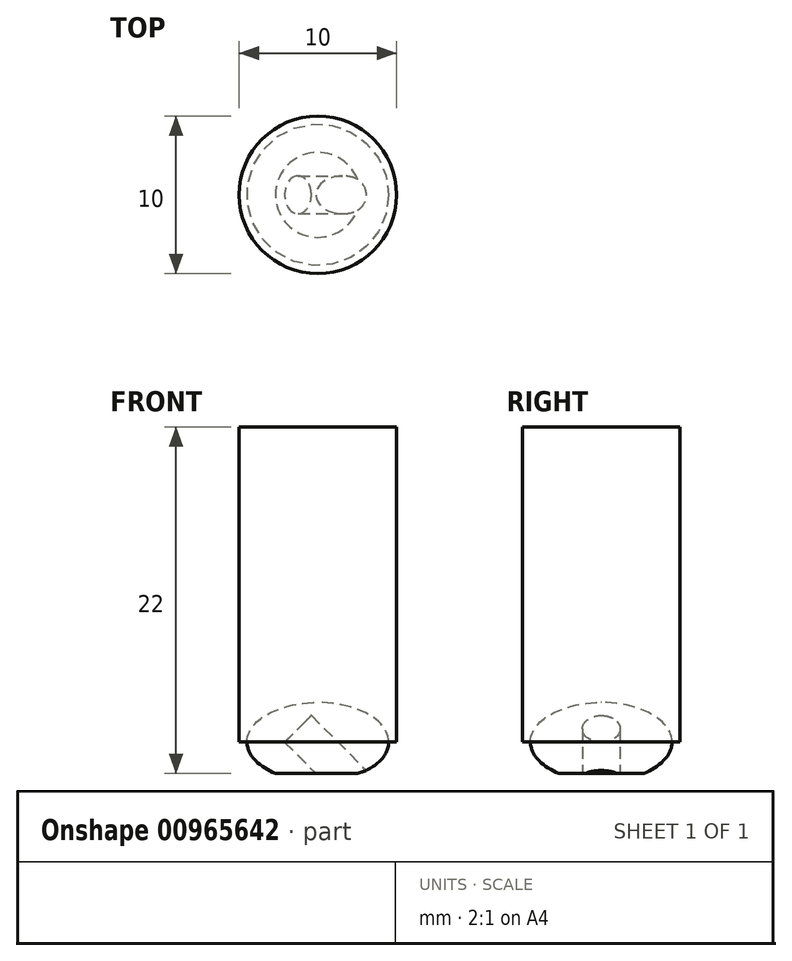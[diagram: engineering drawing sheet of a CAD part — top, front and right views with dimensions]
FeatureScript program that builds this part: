
annotation { "Feature Type Name" : "Feature", "Feature Type Description" : "" }
export const myFeature = defineFeature(function(context is Context, id is Id, definition is map)
    precondition{}
    {
        {
            var Q0;
            Q0=qCreatedBy(makeId("Front.planeOp"),FACE);
            var sketch = newSketch(context, id + "F0", { "sketchPlane" : qUnion([Q0])});
            skEllipse(sketch, "E0", {"center": v(0, 0) * mm, "majorRadius": 4.5 * mm, "minorRadius": 2.5 * mm, "majorAxis": v(1, 0)});
            skLineSegment(sketch, "E1", {"start": v(-2.7, -2) * mm, "end": v(2.7, -2) * mm});
            skLineSegment(sketch, "E2", {"start": v(-1.26, 0.83) * mm, "end": v(3.01, -3.45) * mm, "construction": true});
            skLineSegment(sketch, "E3", {"start": v(-1.26, 0.83) * mm, "end": v(-0.41, 1.68) * mm});
            skLineSegment(sketch, "E4.MirrorCS", {"start": v(-1.26, 0.83) * mm, "end": v(-2.11, -0.02) * mm});
            skLineSegment(sketch, "E5", {"start": v(-0.41, 1.68) * mm, "end": v(3.86, -2.6) * mm});
            skLineSegment(sketch, "E6.MirrorCS", {"start": v(-2.11, -0.02) * mm, "end": v(2.16, -4.3) * mm});
            skPoint(sketch, "E7", {"position": v(1.57, -2) * mm});
            skLineSegment(sketch, "E8", {"start": v(0, 2.5) * mm, "end": v(0, -2) * mm});
            skLineSegment(sketch, "E9", {"start": v(0, -2) * mm, "end": v(0, -2.5) * mm, "construction": true});
            skSolve(sketch);
        }
        {
            var Q0;
            {var subQ0=sQuery(id+"F0.wireOp",EDGE,"E8");var subQ1=sQuery(id+"F0.wireOp",EDGE,"E1");var subQ2=makeQuery(id+"F0.imprint","INTERSECT",VERTEX,{"derivedFrom":[subQ1,subQ0]});Q0=makeQuery(id+"F0.imprint","IMPRINT",FACE,{"disambiguationData":[TD([[makeQuery(id+"F0.imprint","IMPRINT",EDGE,{"disambiguationData":[TD([[subQ2,-1.0]])],"derivedFrom":subQ1}),1.0]])]});}
            var Q1;
            {var subQ0=sQuery(id+"F0.wireOp",EDGE,"E8");var subQ1=sQuery(id+"F0.wireOp",EDGE,"E0");var subQ2=makeQuery(id+"F0.imprint","INTERSECT",VERTEX,{"derivedFrom":[subQ1,subQ0]});Q1=makeQuery(id+"F0.imprint","IMPRINT",FACE,{"disambiguationData":[TD([[makeQuery(id+"F0.imprint","IMPRINT",EDGE,{"disambiguationData":[TD([[subQ2,1.0]])],"derivedFrom":subQ1}),1.0]])]});}
            var Q2;
            {var subQ0=sQuery(id+"F0.wireOp",EDGE,"E5");var subQ3=sQuery(id+"F0.wireOp",EDGE,"E0");var subQ4=makeQuery(id+"F0.imprint","INTERSECT",VERTEX,{"derivedFrom":[subQ3,subQ0]});Q2=makeQuery(id+"F0.imprint","IMPRINT",FACE,{"disambiguationData":[TD([[makeQuery(id+"F0.imprint","IMPRINT",EDGE,{"disambiguationData":[TD([[subQ4,1.0]])],"derivedFrom":subQ3}),1.0]])]});}
            var Q3;
            Q3=sQuery(id+"F0.wireOp",EDGE,"E8");
            revolve(context, id + "F1", {"surfaceOperationType" : NewSurfaceOperationType.NEW, "entities" : qUnion([Q0, Q1, Q2]), "axis" : qUnion([Q3]), "revolveType" : RevolveType.FULL});
        }
        {
            var Q0;
            Q0=sQuery(id+"F0.wireOp",EDGE,"E2");
            var Q1;
            Q1=sQuery(id+"F0.wireOp",VERTEX,"E2.end");
            cPlane(context, id + "F2", {"entities" : qUnion([Q0, Q1]), "cplaneType" : CPlaneType.LINE_POINT, "offset" : 25 * mm, "width" : 150 * mm, "height" : 150 * mm});
        }
        {
            var Q0;
            Q0=qCreatedBy(id+"F2.planeOp",FACE);
            var sketch = newSketch(context, id + "F3", { "sketchPlane" : qUnion([Q0])});
            skCircle(sketch, "E10", {"center": v(0, -0.3) * mm, "radius": 1.2 * mm});
            skSolve(sketch);
        }
        {
            var Q0;
            Q0 = qSketchRegion(id + "F3", true);
            var Q1;
            Q1=sQuery(id+"F0.wireOp",VERTEX,"E2.start");
            extrude(context, id + "F4", {"entities" : qUnion([Q0]), "operationType" : NewBodyOperationType.REMOVE, "endBound" : BoundingType.UP_TO_VERTEX, "oppositeDirection" : true, "depth" : 25 * mm, "endBoundEntityVertex" : qUnion([Q1]), "offsetDistance" : 25 * mm});
        }
        {
            var Q0;
            Q0=qCreatedBy(makeId("Top.planeOp"), FACE);
            var sketch = newSketch(context, id + "F5", { "sketchPlane" : qUnion([Q0])});
            skCircle(sketch, "E11", {"center": v(0, 0) * mm, "radius": 5 * mm});
            skSolve(sketch);
        }
        {
            var Q0;
            Q0 = qSketchRegion(id + "F5", true);
            extrude(context, id + "F6", {"entities" : qUnion([Q0]), "depth" : 20 * mm, "offsetDistance" : 25 * mm});
        }
    });
